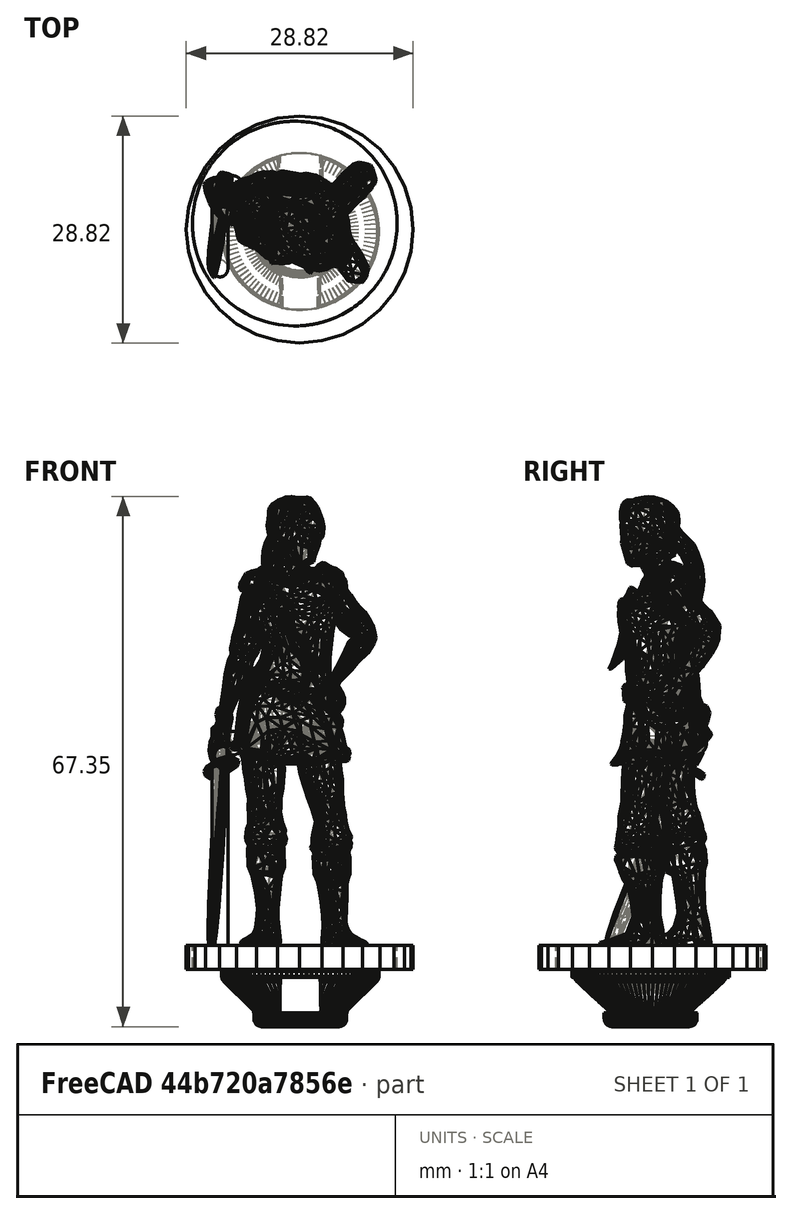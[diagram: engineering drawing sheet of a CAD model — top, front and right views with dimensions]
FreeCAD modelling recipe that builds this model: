
FCSTD DOCUMENT  (FreeCAD 0.17R13541 (Git))
Label: SR4base27-2
License: All rights reserved
LicenseURL: http://en.wikipedia.org/wiki/All_rights_reserved
objects: Part::Feature×5, Part::Cylinder×3, Part::Fuse×3, Mesh::Feature×2, Part::Cut×2, Part::Sphere×1
note: 14 computed .brp shape members not serialized (recipe doc carries the construction recipe); baked Part::Feature solids carry a one-line shape summary decoded from their .brp

FEATURE [Mesh::Feature] FemaleKnight_StandRelaxed_Cleaned4
FEATURE [Part::Feature] FemaleKnight_StandRelaxed_Cleaned4001
  shape: bbox 28.82 x 28.82 x 60.05 mm, 8000 faces, 0 solids (baked)
FEATURE [Part::Feature] FemaleKnight_StandRelaxed_Cleaned4001_solid  label="FemaleKnight_StandRelaxed_Cleaned4001 (Solid)"
  shape: bbox 28.82 x 28.82 x 60.05 mm, 8000 faces (baked)
FEATURE [Part::Cylinder] Cylinder001
  Angle = 360
  AttacherType = Attacher::AttachEngine3D
  Height = 7
  Radius = 13
FEATURE [Part::Cylinder] Cylinder002
  Angle = 360
  AttacherType = Attacher::AttachEngine3D
  Height = 7
  Radius = 16
FEATURE [Part::Cut] Cut
  Base = -> Cylinder002
  Tool = -> Cylinder001
FEATURE [Part::Cut] Cut001
  Base = -> FemaleKnight_StandRelaxed_Cleaned4001_solid
  Tool = -> Cut
FEATURE [Mesh::Feature] Base27
  Placement = pos=(0,0,-7) rot=(0,0,1;0rad)
FEATURE [Part::Feature] Base27001
  shape: bbox 19.99 x 20 x 8 mm, 15618 faces, 0 solids (baked)
FEATURE [Part::Feature] Base27001_solid  label="Base27001 (Solid)"
  Placement = pos=(0.7,-1,0) rot=(0,0,1;0rad)
  shape: bbox 19.99 x 20 x 8 mm, 15618 faces (baked)
FEATURE [Part::Feature] FemaleKnight_StandRelaxed_Cleaned4001_solid001  label="FemaleKnight_StandRelaxed_Cleaned4001 (Solid)001"
  shape: bbox 28.82 x 28.82 x 60.05 mm, 8000 faces (baked)
FEATURE [Part::Cylinder] Cylinder
  Angle = 360
  AttacherType = Attacher::AttachEngine3D
  Height = 32
  Placement = pos=(-9.5,-6.6,1) rot=(1,0,0;-0.366519rad)
  Radius = 1
FEATURE [Part::Sphere] Sphere
  Angle1 = -90
  Angle2 = 90
  Angle3 = 360
  AttacherType = Attacher::AttachEngine3D
  Placement = pos=(-8,4.6,29) rot=(0,0,1;0rad)
  Radius = 1.5
FEATURE [Part::Fuse] Fusion
  Base = -> FemaleKnight_StandRelaxed_Cleaned4001_solid001
  Tool = -> Cylinder
FEATURE [Part::Fuse] Fusion001
  Base = -> Fusion
  Tool = -> Sphere
FEATURE [Part::Fuse] Fusion002
  Base = -> Fusion001
  Tool = -> Base27001_solid
